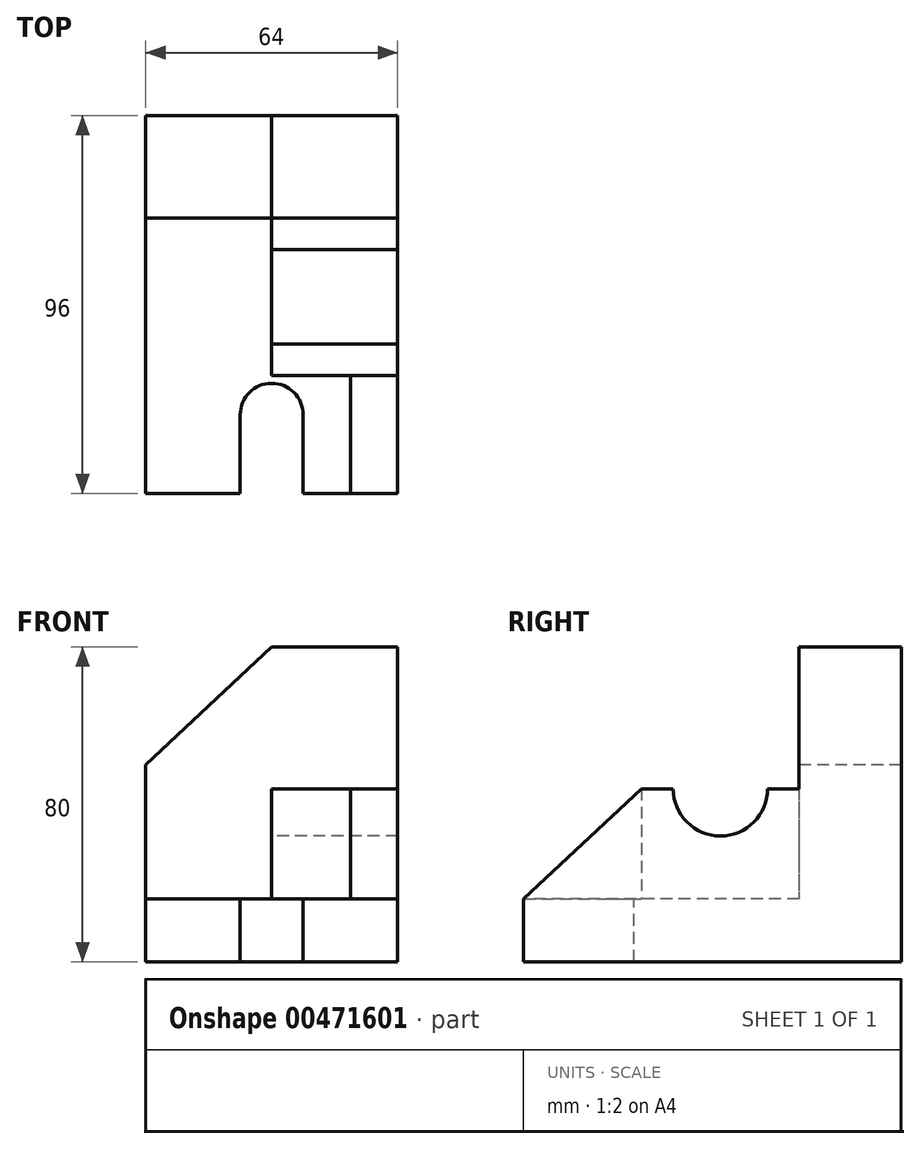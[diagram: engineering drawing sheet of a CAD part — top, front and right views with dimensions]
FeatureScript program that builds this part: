
annotation { "Feature Type Name" : "Feature", "Feature Type Description" : "" }
export const myFeature = defineFeature(function(context is Context, id is Id, definition is map)
    precondition{}
    {
        {
            var Q0;
            Q0=qCreatedBy(makeId("Top.planeOp"),FACE);
            var sketch = newSketch(context, id + "F0", { "sketchPlane" : qUnion([Q0])});
            skLineSegment(sketch, "E0", {"start": v(-25.94, -52.25) * mm, "end": v(38.06, -52.25) * mm});
            skLineSegment(sketch, "E1", {"start": v(38.06, -52.25) * mm, "end": v(38.06, 43.75) * mm});
            skLineSegment(sketch, "E2", {"start": v(38.06, 43.75) * mm, "end": v(-25.94, 43.75) * mm});
            skLineSegment(sketch, "E3", {"start": v(-25.94, 43.75) * mm, "end": v(-25.94, -52.25) * mm});
            skSolve(sketch);
        }
        {
            var Q0;
            Q0 = qSketchRegion(id + "F0", true);
            extrude(context, id + "F1", {"entities" : qUnion([Q0]), "depth" : 16 * mm});
        }
        {
            var Q0;
            Q0=makeQuery(id+"F1.opExtrude","CAP_FACE",FACE,{"disambiguationData":[OSD([sQuery(id+"F0.wireOp",EDGE,"E0"),sQuery(id+"F0.wireOp",EDGE,"E1"),sQuery(id+"F0.wireOp",EDGE,"E2"),sQuery(id+"F0.wireOp",EDGE,"E3")])],"isStart":false});
            var sketch = newSketch(context, id + "F2", { "sketchPlane" : qUnion([Q0])});
            skLineSegment(sketch, "E4", {"start": v(-25.94, -52.25) * mm, "end": v(-1.94, -52.25) * mm});
            skLineSegment(sketch, "E5", {"start": v(-1.94, -52.25) * mm, "end": v(14.06, -52.25) * mm});
            skLineSegment(sketch, "E6", {"start": v(14.06, -52.25) * mm, "end": v(14.06, -32.25) * mm});
            skLineSegment(sketch, "E7", {"start": v(-1.94, -52.25) * mm, "end": v(-1.94, -32.25) * mm});
            skLineSegment(sketch, "E8", {"start": v(14.06, -32.25) * mm, "end": v(-1.94, -32.25) * mm});
            skCircle(sketch, "E9", {"center": v(6.06, -32.25) * mm, "radius": 8 * mm});
            skSolve(sketch);
        }
        {
            var Q0;
            Q0 = qSketchRegion(id + "F2", true);
            extrude(context, id + "F3", {"entities" : qUnion([Q0]), "operationType" : NewBodyOperationType.REMOVE, "oppositeDirection" : true, "depth" : 25 * mm});
        }
        {
            var Q0;
            Q0=makeQuery(id+"F1.opExtrude","CAP_FACE",FACE,{"disambiguationData":[OSD([sQuery(id+"F0.wireOp",EDGE,"E0"),sQuery(id+"F0.wireOp",EDGE,"E1"),sQuery(id+"F0.wireOp",EDGE,"E2"),sQuery(id+"F0.wireOp",EDGE,"E3")])],"isStart":false});
            var sketch = newSketch(context, id + "F4", { "sketchPlane" : qUnion([Q0])});
            skLineSegment(sketch, "E10", {"start": v(38.06, -52.25) * mm, "end": v(26.06, -52.25) * mm});
            skLineSegment(sketch, "E11", {"start": v(26.06, -52.25) * mm, "end": v(26.06, -22.25) * mm});
            skLineSegment(sketch, "E12", {"start": v(26.06, -22.25) * mm, "end": v(38.06, -22.25) * mm});
            skLineSegment(sketch, "E13", {"start": v(38.06, -22.25) * mm, "end": v(38.06, -52.25) * mm});
            skSolve(sketch);
        }
        {
            var Q0;
            Q0 = qSketchRegion(id + "F4", true);
            extrude(context, id + "F5", {"entities" : qUnion([Q0]), "operationType" : NewBodyOperationType.ADD, "depth" : 28 * mm});
        }
        {
            var Q0;
            Q0=makeQuery(id+"F5.opExtrude","SWEPT_FACE",FACE,{"disambiguationData":[OSD([sQuery(id+"F4.wireOp",EDGE,"E11")])]});
            var sketch = newSketch(context, id + "F6", { "sketchPlane" : qUnion([Q0])});
            skLineSegment(sketch, "E14", {"start": v(22.25, 44) * mm, "end": v(52.25, 16) * mm});
            skSolve(sketch);
        }
        {
            var Q0;
            Q0=makeQuery(id+"F6.imprint","IMPRINT",FACE,{"disambiguationData":[TD([[makeQuery(id+"F6.imprint","IMPRINT",EDGE,{"derivedFrom":sQuery(id+"F6.wireOp",EDGE,"E14")}),1.0]])]});
            extrude(context, id + "F7", {"entities" : qUnion([Q0]), "operationType" : NewBodyOperationType.REMOVE, "oppositeDirection" : true, "depth" : 25 * mm});
        }
        {
            var Q0;
            Q0=makeQuery(id+"F1.opExtrude","CAP_FACE",FACE,{"disambiguationData":[OSD([sQuery(id+"F0.wireOp",EDGE,"E0"),sQuery(id+"F0.wireOp",EDGE,"E1"),sQuery(id+"F0.wireOp",EDGE,"E2"),sQuery(id+"F0.wireOp",EDGE,"E3")])],"isStart":false});
            var sketch = newSketch(context, id + "F8", { "sketchPlane" : qUnion([Q0])});
            skLineSegment(sketch, "E15", {"start": v(38.06, -22.25) * mm, "end": v(38.06, 17.75) * mm});
            skLineSegment(sketch, "E16", {"start": v(38.06, 17.75) * mm, "end": v(6.06, 17.75) * mm});
            skPoint(sketch, "E16.endSnap0", {"position": v(6.06, -24.25) * mm});
            skLineSegment(sketch, "E17", {"start": v(6.06, 17.75) * mm, "end": v(6.06, -24.25) * mm});
            skLineSegment(sketch, "E18", {"start": v(38.06, -22.25) * mm, "end": v(6.06, -22.25) * mm});
            skPoint(sketch, "E18.endSnap0", {"position": v(32.06, -22.25) * mm});
            skSolve(sketch);
        }
        {
            var Q0;
            Q0 = qSketchRegion(id + "F8", true);
            extrude(context, id + "F9", {"entities" : qUnion([Q0]), "operationType" : NewBodyOperationType.ADD, "depth" : 28 * mm});
        }
        {
            var Q0;
            Q0=makeQuery(id+"F9.opExtrude","SWEPT_FACE",FACE,{"disambiguationData":[OSD([sQuery(id+"F8.wireOp",EDGE,"E17")])]});
            var sketch = newSketch(context, id + "F10", { "sketchPlane" : qUnion([Q0])});
            skCircle(sketch, "E19", {"center": v(2.25, 44) * mm, "radius": 12 * mm});
            skSolve(sketch);
        }
        {
            var Q0;
            Q0 = qSketchRegion(id + "F10", true);
            extrude(context, id + "F11", {"entities" : qUnion([Q0]), "operationType" : NewBodyOperationType.REMOVE, "oppositeDirection" : true, "depth" : 52 * mm});
        }
        {
            var Q0;
            Q0=makeQuery(id+"F1.opExtrude","CAP_FACE",FACE,{"disambiguationData":[OSD([sQuery(id+"F0.wireOp",EDGE,"E0"),sQuery(id+"F0.wireOp",EDGE,"E1"),sQuery(id+"F0.wireOp",EDGE,"E2"),sQuery(id+"F0.wireOp",EDGE,"E3")])],"isStart":false});
            var sketch = newSketch(context, id + "F12", { "sketchPlane" : qUnion([Q0])});
            skLineSegment(sketch, "E20", {"start": v(-25.94, 43.75) * mm, "end": v(-25.94, 77.75) * mm});
            skLineSegment(sketch, "E21", {"start": v(6.06, 17.75) * mm, "end": v(-25.94, 17.75) * mm});
            skSolve(sketch);
        }
        {
            var Q0;
            Q0 = qSketchRegion(id + "F12", true);
            var Q1;
            {var subQ1=sQuery(id+"F12.wireOp",EDGE,"E21");Q1=makeQuery(id+"F12.imprint","IMPRINT",FACE,{"disambiguationData":[TD([[makeQuery(id+"F12.imprint","IMPRINT",EDGE,{"derivedFrom":subQ1}),-1.0]])]});}
            extrude(context, id + "F13", {"entities" : qUnion([Q0, Q1]), "operationType" : NewBodyOperationType.ADD, "depth" : 64 * mm});
        }
        {
            var Q0;
            Q0=makeQuery(id+"F13.opExtrude","SWEPT_FACE",FACE,{"disambiguationData":[OSD([sQuery(id+"F8.wireOp",EDGE,"E16"),sQuery(id+"F12.wireOp",EDGE,"E21")])]});
            var sketch = newSketch(context, id + "F14", { "sketchPlane" : qUnion([Q0])});
            skLineSegment(sketch, "E22", {"start": v(6.06, 44) * mm, "end": v(6.06, 80) * mm});
            skLineSegment(sketch, "E23", {"start": v(-25.94, 16) * mm, "end": v(-25.94, 50) * mm});
            skLineSegment(sketch, "E24", {"start": v(-25.94, 50) * mm, "end": v(6.06, 80) * mm});
            skSolve(sketch);
        }
        {
            var Q0;
            {var subQ0=sQuery(id+"F14.wireOp",EDGE,"E24");Q0=makeQuery(id+"F14.imprint","IMPRINT",FACE,{"disambiguationData":[TD([[makeQuery(id+"F14.imprint","IMPRINT",EDGE,{"derivedFrom":subQ0}),1.0]])]});}
            extrude(context, id + "F15", {"entities" : qUnion([Q0]), "operationType" : NewBodyOperationType.REMOVE, "oppositeDirection" : true, "depth" : 30 * mm});
        }
    });
